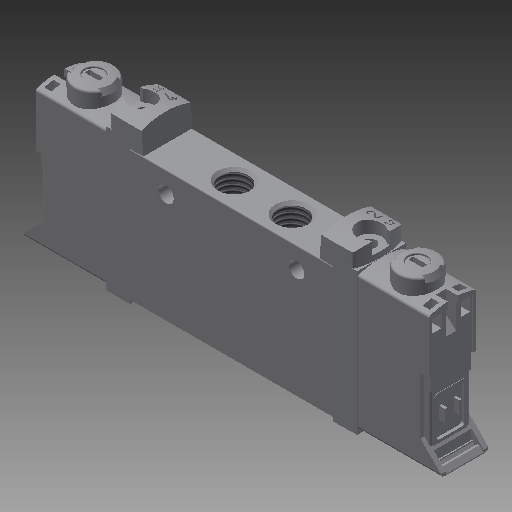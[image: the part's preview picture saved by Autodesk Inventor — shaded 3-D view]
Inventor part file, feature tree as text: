
AUTODESK INVENTOR PART (.ipt)
format: ipt  version: 2018.3 (Build 223284000, 284)  size: 854,528 bytes
history: native  units: mm
features: other x112, sketch x70, extrude x53, revolve x13, hole x4, thread x3
ambient origin geometry x8: Origin, YZ Plane, XZ Plane, XY Plane, X Axis, Y Axis, Z Axis, Center Point
bodies: Solid1 (feature_tree)
feature tree (255):
  extrude  "Extrusion1"  Depth=12.0mm TaperAngle=0.0deg
  extrude  "Extrusion2"  TaperAngle=360.0deg  [1 undecoded]
  extrude  "Extrusion3"  TaperAngle=360.0deg  [1 undecoded]
  sketch  "Sketch_5"  dims[d4=12.0mm d5=0.0mm d6=360.0deg]
  sketch  "Sketch_6"  dims[d7=5.4585mm d8=0.0mm d9=360.0deg]
  sketch  "Sketch_7"  dims[d10=5.4585mm d11=0.0mm d12=360.0deg d13=5.4585mm d14=0.0mm]
  revolve  "Revolution1"  Angle=360.0deg
  thread  "Thread1"  [1 undecoded]
  revolve  "Revolution2"  [1 undecoded]
  thread  "Thread2"  [1 undecoded]
  revolve  "Revolution3"  [1 undecoded]
  thread  "Thread3"  [1 undecoded]
  hole  "Hole1"  [1 undecoded]
  hole  "Hole2"  [1 undecoded]
  hole  "Hole3"  [1 undecoded]
  hole  "Hole4"  [1 undecoded]
  extrude  "Extrusion4"  Depth=5.7mm TaperAngle=0.0deg
  extrude  "Extrusion5"  Depth=4.0mm TaperAngle=0.0deg
  sketch  "Sketch_19"  dims[d57=3.1mm d58=0.0mm d59=0.1mm d60=0.0mm]
  extrude  "Extrusion6"  Depth=5.0mm TaperAngle=0.0deg
  extrude  "Extrusion7"  Depth=12.0mm TaperAngle=0.0deg
  extrude  "Extrusion8"  Depth=3.1mm TaperAngle=0.0deg
  extrude  "Extrusion9"  Depth=1.0mm TaperAngle=0.0deg
  extrude  "Extrusion10"  TaperAngle=360.0deg  [1 undecoded]
  extrude  "Extrusion11"  TaperAngle=360.0deg  [1 undecoded]
  extrude  "Extrusion12"  Depth=3.0mm TaperAngle=0.0deg
  extrude  "Extrusion13"  TaperAngle=360.0deg  [1 undecoded]
  extrude  "Extrusion14"  TaperAngle=360.0deg  [1 undecoded]
  revolve  "Revolution4"  Angle=360.0deg
  extrude  "Extrusion15"  Depth=2.15mm TaperAngle=0.0deg
  extrude  "Extrusion16"  Depth=7.8mm TaperAngle=0.0deg
  extrude  "Extrusion17"  Depth=2.1mm TaperAngle=0.0deg
  extrude  "Extrusion18"  Depth=7.8mm TaperAngle=0.0deg
  extrude  "Extrusion19"  Depth=2.8mm TaperAngle=0.0deg
  extrude  "Extrusion20"  Depth=1.5mm TaperAngle=0.0deg
  extrude  "Extrusion21"  Depth=3.0mm TaperAngle=0.0deg
  extrude  "Extrusion22"  Depth=3.0mm TaperAngle=0.0deg
  extrude  "Extrusion23"  Depth=2.0mm TaperAngle=0.0deg
  extrude  "Extrusion24"  Depth=2.0mm TaperAngle=0.0deg
  extrude  "Extrusion25"  Depth=2.0mm TaperAngle=0.0deg
  extrude  "Extrusion26"  [1 undecoded]
  extrude  "Extrusion27"  [1 undecoded]
  extrude  "Extrusion28"  [1 undecoded]
  revolve  "Revolution5"  [1 undecoded]
  revolve  "Revolution6"  [1 undecoded]
  revolve  "Revolution7"  [1 undecoded]
  sketch  "Sketch_59"
  sketch  "Sketch_56"
  extrude  "Extrusion29"  [1 undecoded]
  extrude  "Extrusion30"  [1 undecoded]
  revolve  "Revolution8"  [1 undecoded]
  revolve  "Revolution9"  [1 undecoded]
  revolve  "Revolution10"  [1 undecoded]
  revolve  "Revolution11"  [1 undecoded]
  revolve  "Revolution12"  [1 undecoded]
  revolve  "Revolution13"  [1 undecoded]
  extrude  "Extrusion31"  [1 undecoded]
  extrude  "Extrusion32"  [1 undecoded]
  extrude  "Extrusion33"  [1 undecoded]
  extrude  "Extrusion34"  [1 undecoded]
  extrude  "Extrusion35"  [1 undecoded]
  extrude  "Extrusion36"  [1 undecoded]
  extrude  "Extrusion37"  [1 undecoded]
  extrude  "Extrusion38"  [1 undecoded]
  extrude  "Extrusion39"  [1 undecoded]
  extrude  "Extrusion40"  [1 undecoded]
  extrude  "Extrusion41"  [1 undecoded]
  extrude  "Extrusion42"  [1 undecoded]
  extrude  "Extrusion43"  [1 undecoded]
  extrude  "Extrusion44"  [1 undecoded]
  extrude  "Extrusion45"  [1 undecoded]
  extrude  "Extrusion46"  [1 undecoded]
  extrude  "Extrusion47"  [1 undecoded]
  extrude  "Extrusion48"  [1 undecoded]
  extrude  "Extrusion49"  [1 undecoded]
  extrude  "Extrusion50"  [1 undecoded]
  extrude  "Extrusion51"  [1 undecoded]
  extrude  "Extrusion52"  [1 undecoded]
  extrude  "Extrusion53"  [1 undecoded]
  other  "DICHTUNG_XY"
  other  "DICHTUNG_YZ"
  other  "DICHTUNG_ZX"
  other  "DICHTUNG_X"
  other  "DICHTUNG_Y"
  other  "DICHTUNG_Z"
  other  "DICHTUNG_Center"
  other  "GEHAUSE_XY"
  other  "GEHAUSE_YZ"
  other  "GEHAUSE_ZX"
  other  "GEHAUSE_X"
  other  "GEHAUSE_Y"
  other  "GEHAUSE_Z"
  other  "GEHAUSE_Center"
  other  "HHB1_XY"
  other  "HHB1_YZ"
  other  "HHB1_ZX"
  other  "HHB1_X"
  other  "HHB1_Y"
  other  "HHB1_Z"
  other  "HHB1_Center"
  other  "HHB2_XY"
  other  "HHB2_YZ"
  other  "HHB2_ZX"
  other  "HHB2_X"
  other  "HHB2_Y"
  other  "HHB2_Z"
  other  "HHB2_Center"
  other  "NEBV1_XY"
  other  "NEBV1_YZ"
  other  "NEBV1_ZX"
  other  "NEBV1_X"
  other  "NEBV1_Y"
  other  "NEBV1_Z"
  other  "NEBV1_Center"
  other  "NEBV2_XY"
  other  "NEBV2_YZ"
  other  "NEBV2_ZX"
  other  "NEBV2_X"
  other  "NEBV2_Y"
  other  "NEBV2_Z"
  other  "NEBV2_Center"
  other  "QS_K1_XY"
  other  "QS_K1_YZ"
  other  "QS_K1_ZX"
  other  "QS_K1_X"
  other  "QS_K1_Y"
  other  "QS_K1_Z"
  other  "QS_K1_Center"
  other  "QS_K1214_XY"
  other  "QS_K1214_YZ"
  other  "QS_K1214_ZX"
  other  "QS_K1214_X"
  other  "QS_K1214_Y"
  other  "QS_K1214_Z"
  other  "QS_K1214_Center"
  other  "QS_K2_XY"
  other  "QS_K2_YZ"
  other  "QS_K2_ZX"
  other  "QS_K2_X"
  other  "QS_K2_Y"
  other  "QS_K2_Z"
  other  "QS_K2_Center"
  other  "QS_K3_XY"
  other  "QS_K3_YZ"
  other  "QS_K3_ZX"
  other  "QS_K3_X"
  other  "QS_K3_Y"
  other  "QS_K3_Z"
  other  "QS_K3_Center"
  other  "QS_K4_XY"
  other  "QS_K4_YZ"
  other  "QS_K4_ZX"
  other  "QS_K4_X"
  other  "QS_K4_Y"
  other  "QS_K4_Z"
  other  "QS_K4_Center"
  other  "QS_K5_XY"
  other  "QS_K5_YZ"
  other  "QS_K5_ZX"
  other  "QS_K5_X"
  other  "QS_K5_Y"
  other  "QS_K5_Z"
  other  "QS_K5_Center"
  other  "SCREW1_XY"
  other  "SCREW1_YZ"
  other  "SCREW1_ZX"
  other  "SCREW1_X"
  other  "SCREW1_Y"
  other  "SCREW1_Z"
  other  "SCREW1_Center"
  other  "SCREW2_XY"
  other  "SCREW2_YZ"
  other  "SCREW2_ZX"
  other  "SCREW2_X"
  other  "SCREW2_Y"
  other  "SCREW2_Z"
  other  "SCREW2_Center"
  other  "VAVE1_XY"
  other  "VAVE1_YZ"
  other  "VAVE1_ZX"
  other  "VAVE1_X"
  other  "VAVE1_Y"
  other  "VAVE1_Z"
  other  "VAVE1_Center"
  other  "VAVE2_XY"
  other  "VAVE2_YZ"
  other  "VAVE2_ZX"
  other  "VAVE2_X"
  other  "VAVE2_Y"
  other  "VAVE2_Z"
  other  "VAVE2_Center"
  sketch  "Sketch_53"  dims[d147=2.0mm d148=0.0mm d149=2.0mm d150=0.0mm]
  sketch  "Sketch_54"  dims[d151=2.0mm d152=0.0mm]
  sketch  "Sketch_55"  dims[d153=0.0mm d154=0.0mm d155=0.0mm d156=0.0mm d157=0.0mm d158=0.0mm d159=0.0mm d160=0.0mm d161=0.0mm d162=0.0mm]
  sketch  "Sketch7"  dims[d15=5.917468mm d16=6.5415mm d17=7.0mm d18=2.0mm d19=90.0deg d20=6.8mm d21=0.0mm]
  sketch  "Sketch8"  dims[d22=5.917468mm d23=6.5415mm d24=7.0mm d25=2.0mm d26=90.0deg d27=6.8mm d28=0.0mm]
  sketch  "Sketch9"  dims[d29=3.0mm d30=6.0mm d31=4.0mm d32=2.0mm d33=90.0deg d34=6.7mm d35=0.0mm]
  sketch  "Sketch10"  dims[d36=3.0mm d37=6.0mm d38=4.0mm d39=2.0mm d40=90.0deg d41=6.7mm d42=0.0mm d43=33.1mm d44=0.0mm d45=5.7mm d46=0.0mm]
  sketch  "Sketch_17"  dims[d53=12.0mm d54=0.0mm d55=12.0mm d56=0.0mm]
  sketch  "Sketch_20"  dims[d61=1.0mm d62=0.0mm d63=2.6mm d64=0.0mm]
  sketch  "Sketch_30"  dims[d97=3.0mm d98=0.0mm d99=3.0mm d100=0.0mm]
  sketch  "Sketch_22"  dims[d68=33.1mm d69=0.0mm d70=5.7mm d71=0.0mm]
  sketch  "Sketch_23"  dims[d72=64.0mm d73=0.0mm d74=4.0mm d75=0.0mm]
  sketch  "Sketch_24"  dims[d76=12.0mm d77=0.0mm d78=5.0mm d79=0.0mm]
  sketch  "Sketch_25"  dims[d80=17.2mm d81=0.0mm d82=12.0mm d83=0.0mm]
  sketch  "Sketch_26"  dims[d84=12.0mm d85=0.0mm d86=3.1mm d87=0.0mm]
  sketch  "Sketch_27"  dims[d88=0.1mm d89=0.0mm d90=1.0mm d91=0.0mm]
  sketch  "Sketch_28"  dims[d92=2.6mm d93=0.0mm d94=360.0deg]
  sketch  "Sketch_29"  dims[d95=360.0deg d96=360.0deg]
  sketch  "Sketch_21"  dims[d65=360.0deg d66=4.0mm d67=0.0mm]
  sketch  "Sketch_31"  dims[d101=360.0deg d102=360.0deg]
  sketch  "Sketch_32"  dims[d103=360.0deg d104=360.0deg]
  sketch  "Sketch_33"  dims[d105=360.0deg d106=360.0deg]
  sketch  "Sketch_119"
  sketch  "Sketch_36"  dims[d111=7.8mm d112=0.0mm d113=7.8mm d114=0.0mm]
  sketch  "Sketch_37"  dims[d115=2.1mm d116=0.0mm d117=2.1mm d118=0.0mm]
  sketch  "Sketch_38"  dims[d119=7.8mm d120=0.0mm d121=7.8mm d122=0.0mm]
  sketch  "Sketch_39"  dims[d123=7.8mm d124=0.0mm d125=2.8mm d126=0.0mm]
  sketch  "Sketch_40"  dims[d127=2.8mm d128=0.0mm d129=1.5mm d130=0.0mm]
  sketch  "Sketch_41"  dims[d131=1.5mm d132=0.0mm d133=3.0mm d134=0.0mm]
  sketch  "Sketch_42"  dims[d135=3.0mm d136=0.0mm d137=3.0mm d138=0.0mm]
  sketch  "Sketch_43"  dims[d139=3.0mm d140=0.0mm d141=2.0mm d142=0.0mm]
  sketch  "Sketch_44"  dims[d143=2.0mm d144=0.0mm d145=2.0mm d146=0.0mm]
  sketch  "Sketch_34"  dims[d107=2.15mm d108=0.0mm d109=2.15mm d110=0.0mm]
  sketch  "Sketch_4"  dims[d0=42.0mm d1=0.0mm d2=12.0mm d3=0.0mm]
  sketch  "Sketch_61"
  sketch  "Sketch_57"
  sketch  "Sketch_62"
  sketch  "Sketch_58"
  sketch  "Sketch_63"
  sketch  "Sketch_64"
  sketch  "Sketch_65"
  sketch  "Sketch_60"
  sketch  "Sketch_66"
  sketch  "Sketch_80"
  sketch  "Sketch_82"
  sketch  "Sketch_84"
  sketch  "Sketch_81"
  sketch  "Sketch_87"
  sketch  "Sketch_88"
  sketch  "Sketch_85"
  sketch  "Sketch_86"
  sketch  "Sketch_94"
  sketch  "Sketch_132"
  sketch  "Sketch_133"
  sketch  "Sketch_134"
  sketch  "Sketch_135"
  sketch  "Sketch_136"
  sketch  "Sketch_137"
  sketch  "Sketch_12"  dims[d47=5.0mm d48=0.0mm d49=12.0mm d50=0.0mm d51=17.2mm d52=0.0mm]
  sketch  "Sketch_68"
  sketch  "Sketch_101"
  sketch  "Sketch_102"
  sketch  "Sketch_103"
  sketch  "Sketch_104"
note: 52 required parameter values undecoded (feature->parameter linkage not recoverable at this tier; creation-order binding heuristic only, values carry confidence <= 0.55)